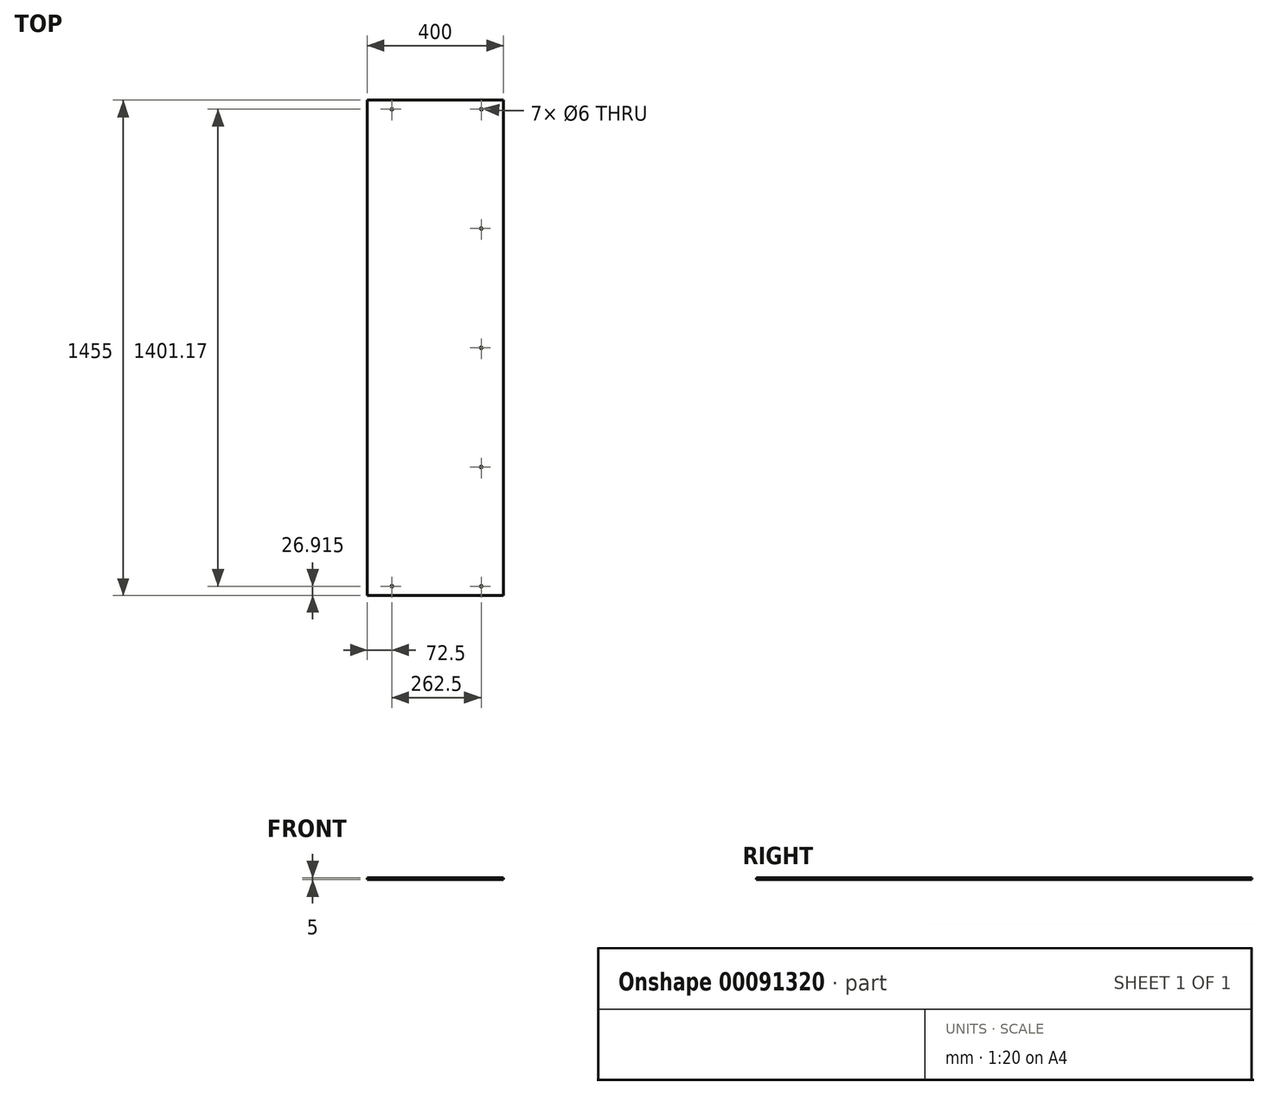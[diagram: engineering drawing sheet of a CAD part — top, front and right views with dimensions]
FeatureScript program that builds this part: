
annotation { "Feature Type Name" : "Feature", "Feature Type Description" : "" }
export const myFeature = defineFeature(function(context is Context, id is Id, definition is map)
    precondition{}
    {
        {
            var Q0;
            Q0=qCreatedBy(makeId("Top.planeOp"),FACE);
            var sketch = newSketch(context, id + "F0", { "sketchPlane" : qUnion([Q0])});
            skLineSegment(sketch, "E0.bottom", {"start": v(200, 727.5) * mm, "end": v(-200, 727.5) * mm});
            skLineSegment(sketch, "E0.top", {"start": v(200, -727.5) * mm, "end": v(-200, -727.5) * mm});
            skLineSegment(sketch, "E0.left", {"start": v(200, 727.5) * mm, "end": v(200, -727.5) * mm});
            skLineSegment(sketch, "E0.right", {"start": v(-200, 727.5) * mm, "end": v(-200, -727.5) * mm});
            skPoint(sketch, "E0.middle", {"position": v(0, 0) * mm});
            skLineSegment(sketch, "E1.bottom", {"start": v(200, -727.5) * mm, "end": v(-55, -727.5) * mm});
            skLineSegment(sketch, "E1.top", {"start": v(200, -777.5) * mm, "end": v(-55, -777.5) * mm});
            skLineSegment(sketch, "E1.left", {"start": v(200, -727.5) * mm, "end": v(200, -777.5) * mm});
            skLineSegment(sketch, "E1.right", {"start": v(-55, -727.5) * mm, "end": v(-55, -777.5) * mm});
            skLineSegment(sketch, "E2.bottom", {"start": v(200, 727.5) * mm, "end": v(-55, 727.5) * mm});
            skLineSegment(sketch, "E2.top", {"start": v(200, 777.5) * mm, "end": v(-55, 777.5) * mm});
            skLineSegment(sketch, "E2.left", {"start": v(200, 727.5) * mm, "end": v(200, 777.5) * mm});
            skLineSegment(sketch, "E2.right", {"start": v(-55, 727.5) * mm, "end": v(-55, 777.5) * mm});
            skSolve(sketch);
        }
        {
            var Q0;
            Q0=makeQuery(id+"F0.imprint","IMPRINT",FACE,{"disambiguationData":[TD([[makeQuery(id+"F0.imprint","IMPRINT",EDGE,{"derivedFrom":sQuery(id+"F0.wireOp",EDGE,"E0.bottom")}),1.0]])]});
            var Q1;
            Q1=makeQuery(id+"F0.imprint","IMPRINT",FACE,{"disambiguationData":[TD([[makeQuery(id+"F0.imprint","IMPRINT",EDGE,{"derivedFrom":sQuery(id+"F0.wireOp",EDGE,"E1.bottom")}),1.0]])]});
            var Q2;
            Q2=makeQuery(id+"F0.imprint","IMPRINT",FACE,{"disambiguationData":[TD([[makeQuery(id+"F0.imprint","IMPRINT",EDGE,{"derivedFrom":sQuery(id+"F0.wireOp",EDGE,"E2.bottom")}),-1.0]])]});
            extrude(context, id + "F1", {"entities" : qUnion([Q0, Q1, Q2]), "depth" : 5 * mm});
        }
        {
            var Q0;
            Q0=makeQuery(id+"F1.opExtrude","CAP_FACE",FACE,{"disambiguationData":[OSD([sQuery(id+"F0.wireOp",EDGE,"E0.bottom"),sQuery(id+"F0.wireOp",EDGE,"E0.top"),sQuery(id+"F0.wireOp",EDGE,"E0.left"),sQuery(id+"F0.wireOp",EDGE,"E0.right"),sQuery(id+"F0.wireOp",EDGE,"E1.top"),sQuery(id+"F0.wireOp",EDGE,"E1.left"),sQuery(id+"F0.wireOp",EDGE,"E1.right"),sQuery(id+"F0.wireOp",EDGE,"E2.top"),sQuery(id+"F0.wireOp",EDGE,"E2.left"),sQuery(id+"F0.wireOp",EDGE,"E2.right")])],"isStart":false});
            var sketch = newSketch(context, id + "F2", { "sketchPlane" : qUnion([Q0])});
            skCircle(sketch, "E3", {"center": v(135, 0) * mm, "radius": 3 * mm});
            skLineSegment(sketch, "E4", {"start": v(-127.5, -727.5) * mm, "end": v(-127.5, -700.58) * mm, "construction": true});
            skLineSegment(sketch, "E5", {"start": v(-127.5, -700.58) * mm, "end": v(200, -700.58) * mm, "construction": true});
            skCircle(sketch, "E6", {"center": v(-127.5, -700.58) * mm, "radius": 3 * mm});
            skLineSegment(sketch, "E7", {"start": v(135, 0) * mm, "end": v(135, -700.58) * mm, "construction": true});
            skCircle(sketch, "E8", {"center": v(135, -700.58) * mm, "radius": 3 * mm});
            skCircle(sketch, "E9", {"center": v(135, -350.3) * mm, "radius": 3 * mm});
            skLineSegment(sketch, "E10", {"start": v(0, 0) * mm, "end": v(230.94, 0) * mm, "construction": true});
            skCircle(sketch, "E11.MirrorC", {"center": v(-127.5, 700.58) * mm, "radius": 3 * mm});
            skCircle(sketch, "E12.MirrorC", {"center": v(135, 700.58) * mm, "radius": 3 * mm});
            skCircle(sketch, "E13.MirrorC", {"center": v(135, 350.3) * mm, "radius": 3 * mm});
            skSolve(sketch);
        }
        {
            var Q0;
            Q0 = qSketchRegion(id + "F2", true);
            extrude(context, id + "F3", {"entities" : qUnion([Q0]), "operationType" : NewBodyOperationType.REMOVE, "endBound" : BoundingType.THROUGH_ALL, "oppositeDirection" : true, "depth" : 25 * mm});
        }
    });
